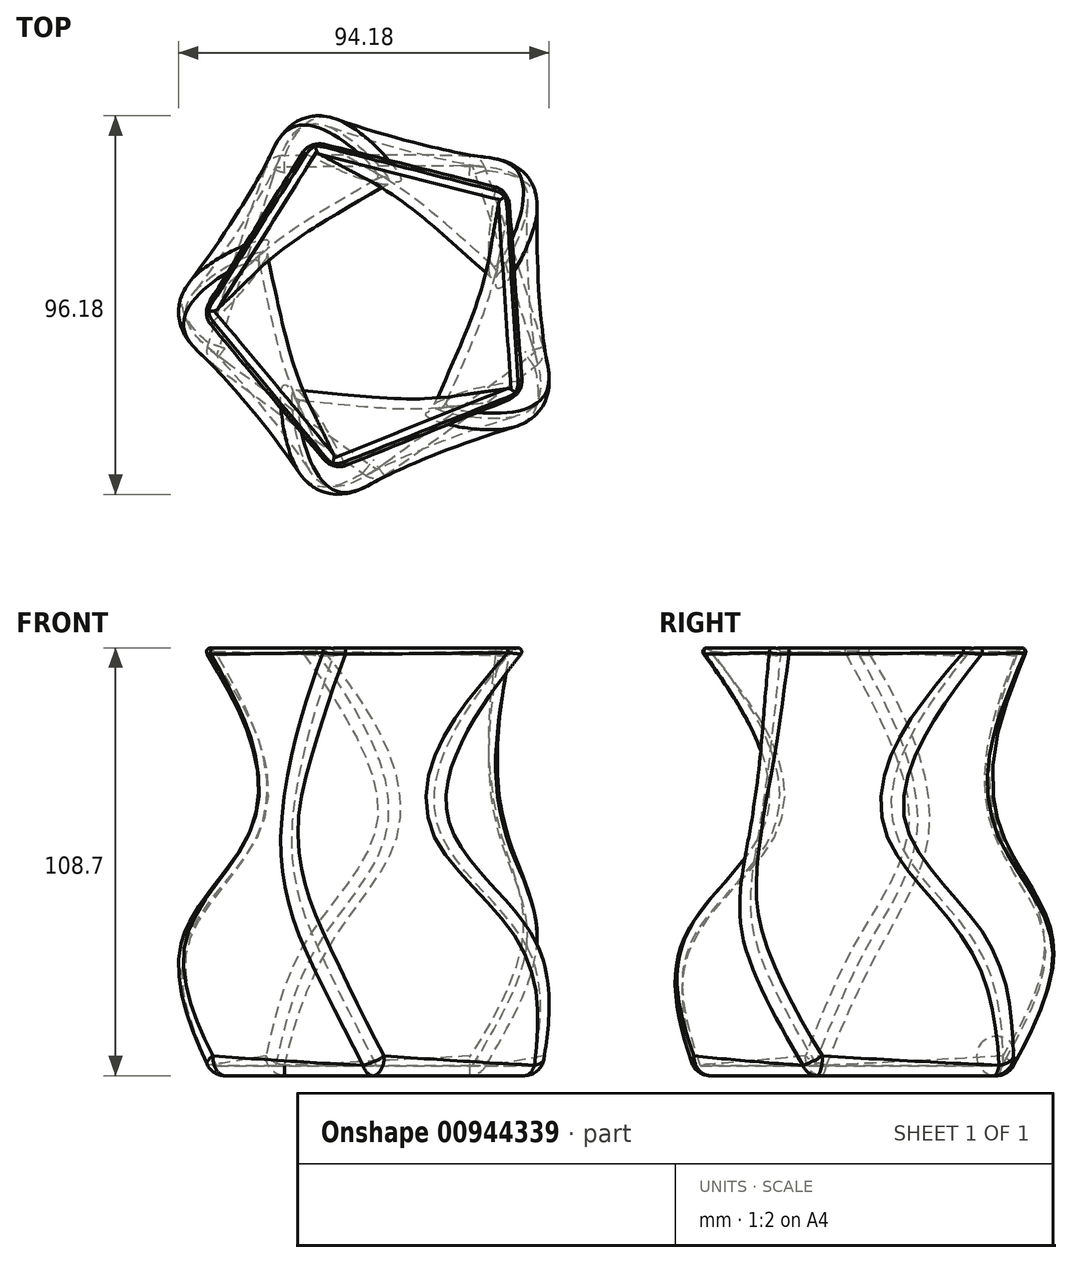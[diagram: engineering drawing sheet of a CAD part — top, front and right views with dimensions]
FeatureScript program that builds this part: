
annotation { "Feature Type Name" : "Feature", "Feature Type Description" : "" }
export const myFeature = defineFeature(function(context is Context, id is Id, definition is map)
    precondition{}
    {
        {
            var Q0;
            Q0=qCreatedBy(makeId("Top.planeOp"),FACE);
            cPlane(context, id + "F0", {"entities" : qUnion([Q0]), "cplaneType" : CPlaneType.OFFSET, "offset" : 35.9 * mm, "width" : 150 * mm, "height" : 150 * mm});
        }
        {
            var Q0;
            Q0=qCreatedBy(id+"F0.planeOp",FACE);
            cPlane(context, id + "F1", {"entities" : qUnion([Q0]), "cplaneType" : CPlaneType.OFFSET, "offset" : 27 * mm, "width" : 150 * mm, "height" : 150 * mm});
        }
        {
            var Q0;
            Q0=qCreatedBy(id+"F1.planeOp",FACE);
            cPlane(context, id + "F2", {"entities" : qUnion([Q0]), "cplaneType" : CPlaneType.OFFSET, "offset" : 45.8 * mm, "width" : 150 * mm, "height" : 150 * mm});
        }
        {
            var Q0;
            Q0=qCreatedBy(makeId("Top.planeOp"),FACE);
            var sketch = newSketch(context, id + "F3", { "sketchPlane" : qUnion([Q0])});
            skCircle(sketch, "E0.cCircle", {"center": v(0, 0) * mm, "radius": 45 * mm, "construction": true});
            skLineSegment(sketch, "E0.0", {"start": v(43.21, -12.56) * mm, "end": v(1.4, -44.98) * mm});
            skLineSegment(sketch, "E0.1", {"start": v(1.4, -44.98) * mm, "end": v(-42.34, -15.23) * mm});
            skLineSegment(sketch, "E0.2", {"start": v(-42.34, -15.23) * mm, "end": v(-27.57, 35.56) * mm});
            skLineSegment(sketch, "E0.3", {"start": v(-27.57, 35.56) * mm, "end": v(25.3, 37.21) * mm});
            skLineSegment(sketch, "E0.4", {"start": v(25.3, 37.21) * mm, "end": v(43.21, -12.56) * mm});
            skSolve(sketch);
        }
        {
            var Q0;
            Q0=qCreatedBy(id+"F0.planeOp",FACE);
            var sketch = newSketch(context, id + "F4", { "sketchPlane" : qUnion([Q0])});
            skCircle(sketch, "E1.cCircle", {"center": v(0, 0) * mm, "radius": 50 * mm, "construction": true});
            skLineSegment(sketch, "E1.0", {"start": v(39.6, -30.52) * mm, "end": v(-16.8, -47.1) * mm});
            skLineSegment(sketch, "E1.1", {"start": v(-16.8, -47.1) * mm, "end": v(-49.98, 1.42) * mm});
            skLineSegment(sketch, "E1.2", {"start": v(-49.98, 1.42) * mm, "end": v(-14.1, 47.97) * mm});
            skLineSegment(sketch, "E1.3", {"start": v(-14.1, 47.97) * mm, "end": v(41.27, 28.23) * mm});
            skLineSegment(sketch, "E1.4", {"start": v(41.27, 28.23) * mm, "end": v(39.6, -30.52) * mm});
            skSolve(sketch);
        }
        {
            var Q0;
            Q0=qCreatedBy(id+"F1.planeOp",FACE);
            var sketch = newSketch(context, id + "F5", { "sketchPlane" : qUnion([Q0])});
            skCircle(sketch, "E2.cCircle", {"center": v(0, 0) * mm, "radius": 35 * mm, "construction": true});
            skLineSegment(sketch, "E2.0", {"start": v(3.25, 34.85) * mm, "end": v(34.15, 7.67) * mm});
            skLineSegment(sketch, "E2.1", {"start": v(34.15, 7.67) * mm, "end": v(17.85, -30.1) * mm});
            skLineSegment(sketch, "E2.2", {"start": v(17.85, -30.1) * mm, "end": v(-23.12, -26.28) * mm});
            skLineSegment(sketch, "E2.3", {"start": v(-23.12, -26.28) * mm, "end": v(-32.14, 13.86) * mm});
            skLineSegment(sketch, "E2.4", {"start": v(-32.14, 13.86) * mm, "end": v(3.25, 34.85) * mm});
            skSolve(sketch);
        }
        {
            var Q0;
            Q0=qCreatedBy(id+"F2.planeOp",FACE);
            var sketch = newSketch(context, id + "F6", { "sketchPlane" : qUnion([Q0])});
            skCircle(sketch, "E3.cCircle", {"center": v(0, 0) * mm, "radius": 45 * mm, "construction": true});
            skLineSegment(sketch, "E3.0", {"start": v(38.59, -23.15) * mm, "end": v(-10.1, -43.85) * mm});
            skLineSegment(sketch, "E3.1", {"start": v(-10.1, -43.85) * mm, "end": v(-44.83, -3.95) * mm});
            skLineSegment(sketch, "E3.2", {"start": v(-44.83, -3.95) * mm, "end": v(-17.6, 41.41) * mm});
            skLineSegment(sketch, "E3.3", {"start": v(-17.6, 41.41) * mm, "end": v(33.94, 29.54) * mm});
            skLineSegment(sketch, "E3.4", {"start": v(33.94, 29.54) * mm, "end": v(38.59, -23.15) * mm});
            skSolve(sketch);
        }
        {
            var Q0;
            Q0=makeQuery(id+"F3.imprint","IMPRINT",FACE,{"disambiguationData":[TD([[makeQuery(id+"F3.imprint","IMPRINT",EDGE,{"derivedFrom":sQuery(id+"F3.wireOp",EDGE,"E0.0")}),-1.0]])]});
            var Q1;
            Q1=makeQuery(id+"F4.imprint","IMPRINT",FACE,{"disambiguationData":[TD([[makeQuery(id+"F4.imprint","IMPRINT",EDGE,{"derivedFrom":sQuery(id+"F4.wireOp",EDGE,"E1.0")}),-1.0]])]});
            var Q2;
            Q2=makeQuery(id+"F5.imprint","IMPRINT",FACE,{"disambiguationData":[TD([[makeQuery(id+"F5.imprint","IMPRINT",EDGE,{"derivedFrom":sQuery(id+"F5.wireOp",EDGE,"E2.0")}),-1.0]])]});
            var Q3;
            Q3=makeQuery(id+"F6.imprint","IMPRINT",FACE,{"disambiguationData":[TD([[makeQuery(id+"F6.imprint","IMPRINT",EDGE,{"derivedFrom":sQuery(id+"F6.wireOp",EDGE,"E3.0")}),-1.0]])]});
            loft(context, id + "F7", {"sheetProfilesArray" : [{ "sheetProfileEntities" : qUnion([Q0]) }, { "sheetProfileEntities" : qUnion([Q1]) }, { "sheetProfileEntities" : qUnion([Q2]) }, { "sheetProfileEntities" : qUnion([Q3]) }]});
        }
        {
            var Q0;
            Q0=makeQuery(id+"F7.opLoft","CAP_FACE",FACE,{"disambiguationData":[OSD([makeQuery(id+"F6.imprint","IMPRINT",FACE,{"disambiguationData":[TD([[makeQuery(id+"F6.imprint","IMPRINT",EDGE,{"derivedFrom":sQuery(id+"F6.wireOp",EDGE,"E3.0")}),-1.0]])]})])],"isStart":true});
            shell(context, id + "F8", {"entities" : qUnion([Q0]), "thickness" : 2.5 * mm});
        }
        {
            var Q0;
            Q0=makeQuery(id+"F7.opLoft","SWEPT_EDGE",EDGE,{"disambiguationData":[OSD([sQuery(id+"F3.wireOp",EDGE,"E0.0"),sQuery(id+"F3.wireOp",EDGE,"E0.4"),sQuery(id+"F4.wireOp",EDGE,"E1.0"),sQuery(id+"F4.wireOp",EDGE,"E1.4"),sQuery(id+"F5.wireOp",EDGE,"E2.1"),sQuery(id+"F5.wireOp",EDGE,"E2.2"),sQuery(id+"F6.wireOp",EDGE,"E3.0"),sQuery(id+"F6.wireOp",EDGE,"E3.4")])]});
            var Q1;
            Q1=makeQuery(id+"F7.opLoft","SWEPT_EDGE",EDGE,{"disambiguationData":[OSD([sQuery(id+"F3.wireOp",EDGE,"E0.0"),sQuery(id+"F3.wireOp",EDGE,"E0.1"),sQuery(id+"F4.wireOp",EDGE,"E1.0"),sQuery(id+"F4.wireOp",EDGE,"E1.1"),sQuery(id+"F5.wireOp",EDGE,"E2.2"),sQuery(id+"F5.wireOp",EDGE,"E2.3"),sQuery(id+"F6.wireOp",EDGE,"E3.0"),sQuery(id+"F6.wireOp",EDGE,"E3.1")])]});
            var Q2;
            Q2=makeQuery(id+"F7.opLoft","SWEPT_EDGE",EDGE,{"disambiguationData":[OSD([sQuery(id+"F3.wireOp",EDGE,"E0.1"),sQuery(id+"F3.wireOp",EDGE,"E0.2"),sQuery(id+"F4.wireOp",EDGE,"E1.1"),sQuery(id+"F4.wireOp",EDGE,"E1.2"),sQuery(id+"F5.wireOp",EDGE,"E2.3"),sQuery(id+"F5.wireOp",EDGE,"E2.4"),sQuery(id+"F6.wireOp",EDGE,"E3.1"),sQuery(id+"F6.wireOp",EDGE,"E3.2")])]});
            var Q3;
            Q3=makeQuery(id+"F7.opLoft","SWEPT_EDGE",EDGE,{"disambiguationData":[OSD([sQuery(id+"F3.wireOp",EDGE,"E0.2"),sQuery(id+"F3.wireOp",EDGE,"E0.3"),sQuery(id+"F4.wireOp",EDGE,"E1.2"),sQuery(id+"F4.wireOp",EDGE,"E1.3"),sQuery(id+"F5.wireOp",EDGE,"E2.0"),sQuery(id+"F5.wireOp",EDGE,"E2.4"),sQuery(id+"F6.wireOp",EDGE,"E3.2"),sQuery(id+"F6.wireOp",EDGE,"E3.3")])]});
            var Q4;
            Q4=makeQuery(id+"F7.opLoft","SWEPT_EDGE",EDGE,{"disambiguationData":[OSD([sQuery(id+"F3.wireOp",EDGE,"E0.3"),sQuery(id+"F3.wireOp",EDGE,"E0.4"),sQuery(id+"F4.wireOp",EDGE,"E1.3"),sQuery(id+"F4.wireOp",EDGE,"E1.4"),sQuery(id+"F5.wireOp",EDGE,"E2.0"),sQuery(id+"F5.wireOp",EDGE,"E2.1"),sQuery(id+"F6.wireOp",EDGE,"E3.3"),sQuery(id+"F6.wireOp",EDGE,"E3.4")])]});
            fillet(context, id + "F9", {"entities" : qUnion([Q0, Q1, Q2, Q3, Q4]), "radius" : 5 * mm, "tangentPropagation" : true, "allowEdgeOverflow" : false});
        }
        {
            var Q0;
            Q0=makeQuery(id+"F7.opLoft","MID_CAP_EDGE",EDGE,{"disambiguationData":[OSD([sQuery(id+"F6.wireOp",EDGE,"E3.0"),sQuery(id+"F6.wireOp",EDGE,"E3.1"),sQuery(id+"F6.wireOp",EDGE,"E3.2")])],"capPos":3.0});
            var Q1;
            Q1=makeQuery(id+"F7.opLoft","MID_CAP_EDGE",EDGE,{"disambiguationData":[OSD([sQuery(id+"F6.wireOp",EDGE,"E3.1"),sQuery(id+"F6.wireOp",EDGE,"E3.2"),sQuery(id+"F6.wireOp",EDGE,"E3.3")])],"capPos":3.0});
            var Q2;
            Q2=makeQuery(id+"F7.opLoft","MID_CAP_EDGE",EDGE,{"disambiguationData":[OSD([sQuery(id+"F6.wireOp",EDGE,"E3.2"),sQuery(id+"F6.wireOp",EDGE,"E3.3"),sQuery(id+"F6.wireOp",EDGE,"E3.4")])],"capPos":3.0});
            var Q3;
            Q3=makeQuery(id+"F7.opLoft","MID_CAP_EDGE",EDGE,{"disambiguationData":[OSD([sQuery(id+"F6.wireOp",EDGE,"E3.0"),sQuery(id+"F6.wireOp",EDGE,"E3.1"),sQuery(id+"F6.wireOp",EDGE,"E3.4")])],"capPos":3.0});
            var Q4;
            Q4=makeQuery(id+"F7.opLoft","MID_CAP_EDGE",EDGE,{"disambiguationData":[OSD([sQuery(id+"F6.wireOp",EDGE,"E3.0"),sQuery(id+"F6.wireOp",EDGE,"E3.3"),sQuery(id+"F6.wireOp",EDGE,"E3.4")])],"capPos":3.0});
            var Q5;
            {var subQ0=sQuery(id+"F6.wireOp",EDGE,"E3.3");var subQ1=sQuery(id+"F6.wireOp",EDGE,"E3.2");Q5=makeQuery(id+"F9.opFillet","BLEND_EDGE",EDGE,{"blendedFrom":[makeQuery(id+"F7.opLoft","SWEPT_EDGE",EDGE,{"disambiguationData":[OSD([sQuery(id+"F3.wireOp",EDGE,"E0.2"),sQuery(id+"F3.wireOp",EDGE,"E0.3"),sQuery(id+"F4.wireOp",EDGE,"E1.2"),sQuery(id+"F4.wireOp",EDGE,"E1.3"),sQuery(id+"F5.wireOp",EDGE,"E2.0"),sQuery(id+"F5.wireOp",EDGE,"E2.4"),subQ1,subQ0])]}),makeQuery(id+"F7.opLoft","CAP_FACE",FACE,{"disambiguationData":[OSD([makeQuery(id+"F6.imprint","IMPRINT",FACE,{"disambiguationData":[TD([[makeQuery(id+"F6.imprint","IMPRINT",EDGE,{"derivedFrom":sQuery(id+"F6.wireOp",EDGE,"E3.0")}),-1.0]])]})])],"isStart":true})],"blendedInto":[makeQuery(id+"F7.opLoft","CAP_FACE",FACE,{"disambiguationData":[OSD([makeQuery(id+"F6.imprint","IMPRINT",FACE,{"disambiguationData":[TD([[makeQuery(id+"F6.imprint","IMPRINT",EDGE,{"derivedFrom":sQuery(id+"F6.wireOp",EDGE,"E3.0")}),-1.0]])]})])],"isStart":true})]});}
            var Q6;
            {var subQ0=sQuery(id+"F6.wireOp",EDGE,"E3.2");var subQ1=sQuery(id+"F6.wireOp",EDGE,"E3.1");Q6=makeQuery(id+"F9.opFillet","BLEND_EDGE",EDGE,{"blendedFrom":[makeQuery(id+"F7.opLoft","SWEPT_EDGE",EDGE,{"disambiguationData":[OSD([sQuery(id+"F3.wireOp",EDGE,"E0.1"),sQuery(id+"F3.wireOp",EDGE,"E0.2"),sQuery(id+"F4.wireOp",EDGE,"E1.1"),sQuery(id+"F4.wireOp",EDGE,"E1.2"),sQuery(id+"F5.wireOp",EDGE,"E2.3"),sQuery(id+"F5.wireOp",EDGE,"E2.4"),subQ1,subQ0])]}),makeQuery(id+"F7.opLoft","CAP_FACE",FACE,{"disambiguationData":[OSD([makeQuery(id+"F6.imprint","IMPRINT",FACE,{"disambiguationData":[TD([[makeQuery(id+"F6.imprint","IMPRINT",EDGE,{"derivedFrom":sQuery(id+"F6.wireOp",EDGE,"E3.0")}),-1.0]])]})])],"isStart":true})],"blendedInto":[makeQuery(id+"F7.opLoft","CAP_FACE",FACE,{"disambiguationData":[OSD([makeQuery(id+"F6.imprint","IMPRINT",FACE,{"disambiguationData":[TD([[makeQuery(id+"F6.imprint","IMPRINT",EDGE,{"derivedFrom":sQuery(id+"F6.wireOp",EDGE,"E3.0")}),-1.0]])]})])],"isStart":true})]});}
            var Q7;
            {var subQ0=sQuery(id+"F6.wireOp",EDGE,"E3.3");var subQ1=sQuery(id+"F6.wireOp",EDGE,"E3.4");Q7=makeQuery(id+"F9.opFillet","BLEND_EDGE",EDGE,{"blendedFrom":[makeQuery(id+"F7.opLoft","SWEPT_EDGE",EDGE,{"disambiguationData":[OSD([sQuery(id+"F3.wireOp",EDGE,"E0.3"),sQuery(id+"F3.wireOp",EDGE,"E0.4"),sQuery(id+"F4.wireOp",EDGE,"E1.3"),sQuery(id+"F4.wireOp",EDGE,"E1.4"),sQuery(id+"F5.wireOp",EDGE,"E2.0"),sQuery(id+"F5.wireOp",EDGE,"E2.1"),subQ0,subQ1])]}),makeQuery(id+"F7.opLoft","CAP_FACE",FACE,{"disambiguationData":[OSD([makeQuery(id+"F6.imprint","IMPRINT",FACE,{"disambiguationData":[TD([[makeQuery(id+"F6.imprint","IMPRINT",EDGE,{"derivedFrom":sQuery(id+"F6.wireOp",EDGE,"E3.0")}),-1.0]])]})])],"isStart":true})],"blendedInto":[makeQuery(id+"F7.opLoft","CAP_FACE",FACE,{"disambiguationData":[OSD([makeQuery(id+"F6.imprint","IMPRINT",FACE,{"disambiguationData":[TD([[makeQuery(id+"F6.imprint","IMPRINT",EDGE,{"derivedFrom":sQuery(id+"F6.wireOp",EDGE,"E3.0")}),-1.0]])]})])],"isStart":true})]});}
            var Q8;
            {var subQ0=sQuery(id+"F6.wireOp",EDGE,"E3.0");var subQ1=sQuery(id+"F6.wireOp",EDGE,"E3.4");Q8=makeQuery(id+"F9.opFillet","BLEND_EDGE",EDGE,{"blendedFrom":[makeQuery(id+"F7.opLoft","SWEPT_EDGE",EDGE,{"disambiguationData":[OSD([sQuery(id+"F3.wireOp",EDGE,"E0.0"),sQuery(id+"F3.wireOp",EDGE,"E0.4"),sQuery(id+"F4.wireOp",EDGE,"E1.0"),sQuery(id+"F4.wireOp",EDGE,"E1.4"),sQuery(id+"F5.wireOp",EDGE,"E2.1"),sQuery(id+"F5.wireOp",EDGE,"E2.2"),subQ0,subQ1])]}),makeQuery(id+"F7.opLoft","CAP_FACE",FACE,{"disambiguationData":[OSD([makeQuery(id+"F6.imprint","IMPRINT",FACE,{"disambiguationData":[TD([[makeQuery(id+"F6.imprint","IMPRINT",EDGE,{"derivedFrom":subQ0}),-1.0]])]})])],"isStart":true})],"blendedInto":[makeQuery(id+"F7.opLoft","CAP_FACE",FACE,{"disambiguationData":[OSD([makeQuery(id+"F6.imprint","IMPRINT",FACE,{"disambiguationData":[TD([[makeQuery(id+"F6.imprint","IMPRINT",EDGE,{"derivedFrom":subQ0}),-1.0]])]})])],"isStart":true})]});}
            fillet(context, id + "F10", {"entities" : qUnion([Q0, Q1, Q2, Q3, Q4, Q5, Q6, Q7, Q8]), "radius" : 1 * mm, "tangentPropagation" : true, "allowEdgeOverflow" : false});
        }
        {
            var Q0;
            Q0=makeQuery(id+"F8.opShell","OFFSET_EDGE",EDGE,{"disambiguationData":[OSD([sQuery(id+"F6.wireOp",EDGE,"E3.0"),sQuery(id+"F6.wireOp",EDGE,"E3.3"),sQuery(id+"F6.wireOp",EDGE,"E3.4")])]});
            var Q1;
            Q1=makeQuery(id+"F8.opShell","OFFSET_EDGE",EDGE,{"disambiguationData":[OSD([sQuery(id+"F6.wireOp",EDGE,"E3.2"),sQuery(id+"F6.wireOp",EDGE,"E3.3"),sQuery(id+"F6.wireOp",EDGE,"E3.4")])]});
            var Q2;
            Q2=makeQuery(id+"F8.opShell","OFFSET_EDGE",EDGE,{"disambiguationData":[OSD([sQuery(id+"F6.wireOp",EDGE,"E3.0"),sQuery(id+"F6.wireOp",EDGE,"E3.1"),sQuery(id+"F6.wireOp",EDGE,"E3.4")])]});
            var Q3;
            Q3=makeQuery(id+"F8.opShell","OFFSET_EDGE",EDGE,{"disambiguationData":[OSD([sQuery(id+"F6.wireOp",EDGE,"E3.0"),sQuery(id+"F6.wireOp",EDGE,"E3.1"),sQuery(id+"F6.wireOp",EDGE,"E3.2")])]});
            var Q4;
            Q4=makeQuery(id+"F8.opShell","OFFSET_EDGE",EDGE,{"disambiguationData":[OSD([sQuery(id+"F6.wireOp",EDGE,"E3.1"),sQuery(id+"F6.wireOp",EDGE,"E3.2"),sQuery(id+"F6.wireOp",EDGE,"E3.3")])]});
            fillet(context, id + "F11", {"entities" : qUnion([Q0, Q1, Q2, Q3, Q4]), "radius" : 2.5 * mm, "tangentPropagation" : true, "allowEdgeOverflow" : false});
        }
        {
            var Q0;
            Q0=makeQuery(id+"F7.opLoft","MID_CAP_EDGE",EDGE,{"disambiguationData":[OSD([sQuery(id+"F3.wireOp",EDGE,"E0.2"),sQuery(id+"F3.wireOp",EDGE,"E0.3"),sQuery(id+"F3.wireOp",EDGE,"E0.4")])],"capPos":0.0});
            fillet(context, id + "F12", {"entities" : qUnion([Q0]), "radius" : 5 * mm, "tangentPropagation" : true, "allowEdgeOverflow" : false});
        }
    });
